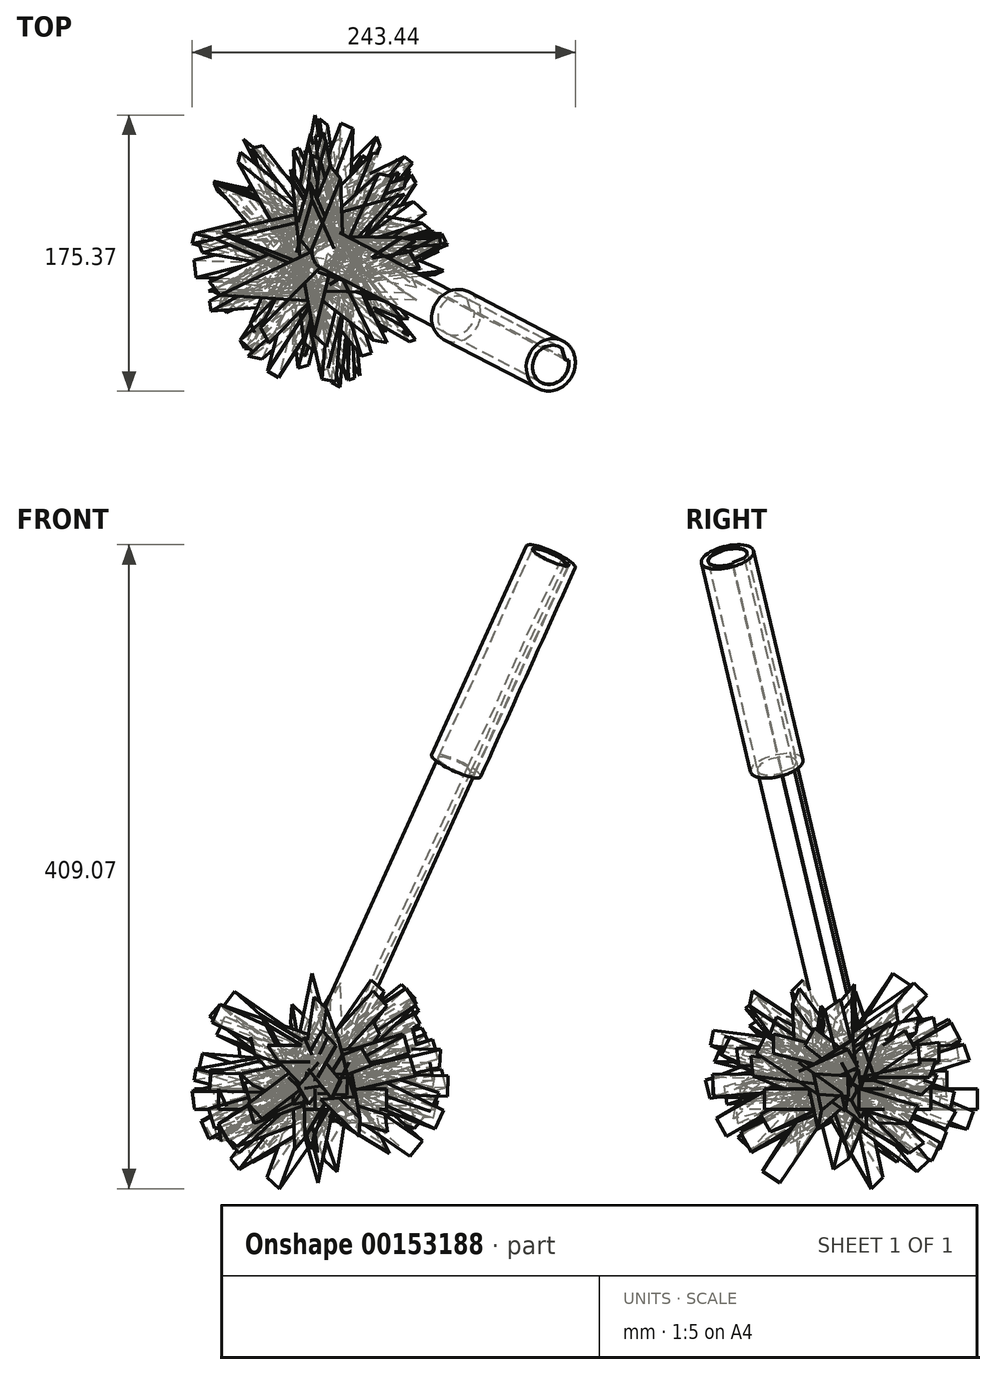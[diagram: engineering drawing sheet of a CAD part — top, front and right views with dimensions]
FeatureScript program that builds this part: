
annotation { "Feature Type Name" : "Feature", "Feature Type Description" : "" }
export const myFeature = defineFeature(function(context is Context, id is Id, definition is map)
    precondition{}
    {
        {
            var Q0;
            Q0=qCreatedBy(makeId("Top.planeOp"),FACE);
            var sketch = newSketch(context, id + "F0", { "sketchPlane" : qUnion([Q0])});
            skCircle(sketch, "E0", {"center": v(0, 0) * mm, "radius": 20.07 * mm});
            skSolve(sketch);
        }
        {
            var Q0;
            Q0=makeQuery(id+"F0.imprint","IMPRINT",FACE,{"disambiguationData":[TD([[makeQuery(id+"F0.imprint","IMPRINT",EDGE,{"derivedFrom":sQuery(id+"F0.wireOp",EDGE,"E0")}),1.0]])]});
            extrude(context, id + "F1", {"entities" : qUnion([Q0]), "depth" : 13.14 * mm});
        }
        {
            var Q0;
            Q0=makeQuery(id+"F1.opExtrude","CAP_FACE",FACE,{"disambiguationData":[OSD([sQuery(id+"F0.wireOp",EDGE,"E0")])],"isStart":false});
            var sketch = newSketch(context, id + "F2", { "sketchPlane" : qUnion([Q0])});
            skLineSegment(sketch, "E1", {"start": v(0, 20.07) * mm, "end": v(0, 75.25) * mm});
            skLineSegment(sketch, "E2", {"start": v(0, 75.25) * mm, "end": v(-12, 16.08) * mm});
            skLineSegment(sketch, "E3", {"start": v(-12, 16.08) * mm, "end": v(12, 16.08) * mm});
            skLineSegment(sketch, "E4", {"start": v(12, 16.08) * mm, "end": v(0, 75.25) * mm});
            skSolve(sketch);
        }
        {
            var Q0;
            {var subQ0=sQuery(id+"F2.wireOp",EDGE,"E1");Q0=makeQuery(id+"F2.imprint","IMPRINT",FACE,{"disambiguationData":[TD([[makeQuery(id+"F2.imprint","IMPRINT",EDGE,{"derivedFrom":subQ0}),1.0]])]});}
            var Q1;
            {var subQ0=sQuery(id+"F2.wireOp",EDGE,"E1");Q1=makeQuery(id+"F2.imprint","IMPRINT",FACE,{"disambiguationData":[TD([[makeQuery(id+"F2.imprint","IMPRINT",EDGE,{"derivedFrom":subQ0}),-1.0]])]});}
            extrude(context, id + "F3", {"entities" : qUnion([Q0, Q1]), "operationType" : NewBodyOperationType.ADD, "oppositeDirection" : true, "depth" : 13.16 * mm});
        }
        {
            var Q0;
            {var subQ0=sQuery(id+"F0.wireOp",EDGE,"E0");Q0=makeQuery(id+"F3.boolean.opBoolean","MERGE",FACE,{"derivedFrom":[makeQuery(id+"F1.opExtrude","CAP_FACE",FACE,{"disambiguationData":[OSD([subQ0])],"isStart":false}),makeQuery(id+"F3.opExtrude","CAP_FACE",FACE,{"disambiguationData":[OSD([subQ0,sQuery(id+"F2.wireOp",EDGE,"E2"),sQuery(id+"F2.wireOp",EDGE,"E4")])],"isStart":true})]});}
            var sketch = newSketch(context, id + "F4", { "sketchPlane" : qUnion([Q0])});
            skLineSegment(sketch, "E5", {"start": v(-12, -16.08) * mm, "end": v(0, -75.25) * mm});
            skLineSegment(sketch, "E6", {"start": v(0, -75.25) * mm, "end": v(12, -16.08) * mm});
            skLineSegment(sketch, "E7", {"start": v(12, -16.08) * mm, "end": v(-12, -16.08) * mm});
            skSolve(sketch);
        }
        {
            var Q0;
            {var subQ0=sQuery(id+"F4.wireOp",EDGE,"E5");Q0=makeQuery(id+"F4.imprint","IMPRINT",FACE,{"disambiguationData":[TD([[makeQuery(id+"F4.imprint","IMPRINT",EDGE,{"derivedFrom":subQ0}),1.0]])]});}
            extrude(context, id + "F5", {"entities" : qUnion([Q0]), "operationType" : NewBodyOperationType.ADD, "oppositeDirection" : true, "depth" : 13.14 * mm});
        }
        {
            var Q0;
            {var subQ0=sQuery(id+"F0.wireOp",EDGE,"E0");Q0=makeQuery(id+"F5.boolean.opBoolean","MERGE",FACE,{"derivedFrom":[makeQuery(id+"F3.boolean.opBoolean","MERGE",FACE,{"derivedFrom":[makeQuery(id+"F1.opExtrude","CAP_FACE",FACE,{"disambiguationData":[OSD([subQ0])],"isStart":false}),makeQuery(id+"F3.opExtrude","CAP_FACE",FACE,{"disambiguationData":[OSD([subQ0,sQuery(id+"F2.wireOp",EDGE,"E2"),sQuery(id+"F2.wireOp",EDGE,"E4")])],"isStart":true})]}),makeQuery(id+"F5.opExtrude","CAP_FACE",FACE,{"disambiguationData":[OSD([subQ0,sQuery(id+"F4.wireOp",EDGE,"E5"),sQuery(id+"F4.wireOp",EDGE,"E6")])],"isStart":true})]});}
            var sketch = newSketch(context, id + "F6", { "sketchPlane" : qUnion([Q0])});
            skLineSegment(sketch, "E8", {"start": v(-12, 16.08) * mm, "end": v(-76.5, 0) * mm});
            skLineSegment(sketch, "E9", {"start": v(-76.5, 0) * mm, "end": v(-12, -16.08) * mm});
            skLineSegment(sketch, "E10", {"start": v(-12, -16.08) * mm, "end": v(-12, 16.08) * mm});
            skSolve(sketch);
        }
        {
            var Q0;
            Q0=makeQuery(id+"F6.imprint","IMPRINT",FACE,{"disambiguationData":[TD([[makeQuery(id+"F6.imprint","IMPRINT",EDGE,{"derivedFrom":sQuery(id+"F6.wireOp",EDGE,"E8")}),1.0]])]});
            extrude(context, id + "F7", {"entities" : qUnion([Q0]), "operationType" : NewBodyOperationType.ADD, "oppositeDirection" : true, "depth" : 13.1 * mm});
        }
        {
            var Q0;
            {var subQ0=sQuery(id+"F0.wireOp",EDGE,"E0");Q0=makeQuery(id+"F7.boolean.opBoolean","MERGE",FACE,{"derivedFrom":[makeQuery(id+"F5.boolean.opBoolean","MERGE",FACE,{"derivedFrom":[makeQuery(id+"F3.boolean.opBoolean","MERGE",FACE,{"derivedFrom":[makeQuery(id+"F1.opExtrude","CAP_FACE",FACE,{"disambiguationData":[OSD([subQ0])],"isStart":false}),makeQuery(id+"F3.opExtrude","CAP_FACE",FACE,{"disambiguationData":[OSD([subQ0,sQuery(id+"F2.wireOp",EDGE,"E2"),sQuery(id+"F2.wireOp",EDGE,"E4")])],"isStart":true})]}),makeQuery(id+"F5.opExtrude","CAP_FACE",FACE,{"disambiguationData":[OSD([subQ0,sQuery(id+"F4.wireOp",EDGE,"E5"),sQuery(id+"F4.wireOp",EDGE,"E6")])],"isStart":true})]}),makeQuery(id+"F7.opExtrude","CAP_FACE",FACE,{"disambiguationData":[OSD([subQ0,sQuery(id+"F6.wireOp",EDGE,"E8"),sQuery(id+"F6.wireOp",EDGE,"E9")])],"isStart":true})]});}
            var sketch = newSketch(context, id + "F8", { "sketchPlane" : qUnion([Q0])});
            skLineSegment(sketch, "E11", {"start": v(12, 16.08) * mm, "end": v(75.98, 0) * mm});
            skLineSegment(sketch, "E12", {"start": v(75.98, 0) * mm, "end": v(12, -16.08) * mm});
            skSolve(sketch);
        }
        {
            var Q0;
            Q0=makeQuery(id+"F8.imprint","IMPRINT",FACE,{"disambiguationData":[TD([[makeQuery(id+"F8.imprint","IMPRINT",EDGE,{"derivedFrom":sQuery(id+"F8.wireOp",EDGE,"E11")}),-1.0]])]});
            extrude(context, id + "F9", {"entities" : qUnion([Q0]), "operationType" : NewBodyOperationType.ADD, "oppositeDirection" : true, "depth" : 13.05 * mm});
        }
        {
            var Q0;
            {var subQ0=sQuery(id+"F0.wireOp",EDGE,"E0");Q0=makeQuery(id+"F9.boolean.opBoolean","MERGE",FACE,{"derivedFrom":[makeQuery(id+"F7.boolean.opBoolean","MERGE",FACE,{"derivedFrom":[makeQuery(id+"F5.boolean.opBoolean","MERGE",FACE,{"derivedFrom":[makeQuery(id+"F3.boolean.opBoolean","MERGE",FACE,{"derivedFrom":[makeQuery(id+"F1.opExtrude","CAP_FACE",FACE,{"disambiguationData":[OSD([subQ0])],"isStart":false}),makeQuery(id+"F3.opExtrude","CAP_FACE",FACE,{"disambiguationData":[OSD([subQ0,sQuery(id+"F2.wireOp",EDGE,"E2"),sQuery(id+"F2.wireOp",EDGE,"E4")])],"isStart":true})]}),makeQuery(id+"F5.opExtrude","CAP_FACE",FACE,{"disambiguationData":[OSD([subQ0,sQuery(id+"F4.wireOp",EDGE,"E5"),sQuery(id+"F4.wireOp",EDGE,"E6")])],"isStart":true})]}),makeQuery(id+"F7.opExtrude","CAP_FACE",FACE,{"disambiguationData":[OSD([subQ0,sQuery(id+"F6.wireOp",EDGE,"E8"),sQuery(id+"F6.wireOp",EDGE,"E9")])],"isStart":true})]}),makeQuery(id+"F9.opExtrude","CAP_FACE",FACE,{"disambiguationData":[OSD([subQ0,sQuery(id+"F8.wireOp",EDGE,"E11"),sQuery(id+"F8.wireOp",EDGE,"E12")])],"isStart":true})]});}
            var sketch = newSketch(context, id + "F10", { "sketchPlane" : qUnion([Q0])});
            skCircle(sketch, "E13", {"center": v(0, 0) * mm, "radius": 20.07 * mm});
            skSolve(sketch);
        }
        {
            var Q0;
            Q0=makeQuery(id+"F1.opExtrude","CAP_FACE",FACE,{"disambiguationData":[OSD([sQuery(id+"F0.wireOp",EDGE,"E0")])],"isStart":true});
            var sketch = newSketch(context, id + "F11", { "sketchPlane" : qUnion([Q0])});
            skCircle(sketch, "E14", {"center": v(0, 0) * mm, "radius": 20.07 * mm});
            skSolve(sketch);
        }
        {
            var Q0;
            Q0=makeQuery(id+"F1.opExtrude","SWEPT_BODY",BODY,{"disambiguationData":[OSD([sQuery(id+"F0.wireOp",EDGE,"E0")])]});
            var Q1;
            Q1=sQuery(id+"F10.wireOp",EDGE,"E13");
            circularPattern(context, id + "F12", {"entities" : qUnion([Q0]), "axis" : qUnion([Q1]), "angle" : 37 * degree, "instanceCount" : 2});
        }
        {
            var Q0;
            Q0=makeQuery(id+"F1.opExtrude","SWEPT_BODY",BODY,{"disambiguationData":[OSD([sQuery(id+"F0.wireOp",EDGE,"E0")])]});
            var Q1;
            Q1=makeQuery(id+"F12.opPattern","COPY",BODY,{"derivedFrom":makeQuery(id+"F1.opExtrude","SWEPT_BODY",BODY,{"disambiguationData":[OSD([sQuery(id+"F0.wireOp",EDGE,"E0")])]}),"instanceName":"1"});
            var Q2;
            Q2=makeQuery(id+"F12.opPattern","COPY",EDGE,{"derivedFrom":makeQuery(id+"F7.opExtrude","CAP_EDGE",EDGE,{"disambiguationData":[OSD([sQuery(id+"F6.wireOp",EDGE,"E8")])],"isStart":true}),"instanceName":"1"});
            circularPattern(context, id + "F13", {"entities" : qUnion([Q0, Q1]), "axis" : qUnion([Q2]), "angle" : 30 * degree, "instanceCount" : 2});
        }
        {
            var Q0;
            Q0=makeQuery(id+"F1.opExtrude","SWEPT_BODY",BODY,{"disambiguationData":[OSD([sQuery(id+"F0.wireOp",EDGE,"E0")])]});
            var Q1;
            Q1=makeQuery(id+"F12.opPattern","COPY",EDGE,{"derivedFrom":makeQuery(id+"F7.opExtrude","CAP_EDGE",EDGE,{"disambiguationData":[OSD([sQuery(id+"F6.wireOp",EDGE,"E9")])],"isStart":false}),"instanceName":"1"});
            circularPattern(context, id + "F14", {"entities" : qUnion([Q0]), "axis" : qUnion([Q1]), "angle" : 30 * degree, "instanceCount" : 2});
        }
        {
            var Q0;
            Q0=makeQuery(id+"F13.opPattern","COPY",BODY,{"derivedFrom":makeQuery(id+"F1.opExtrude","SWEPT_BODY",BODY,{"disambiguationData":[OSD([sQuery(id+"F0.wireOp",EDGE,"E0")])]}),"instanceName":"1"});
            var Q1;
            Q1=sQuery(id+"F11.wireOp",EDGE,"E14");
            circularPattern(context, id + "F15", {"entities" : qUnion([Q0]), "axis" : qUnion([Q1]), "angle" : 30 * degree, "instanceCount" : 2});
        }
        {
            var Q0;
            Q0=makeQuery(id+"F14.opPattern","COPY",BODY,{"derivedFrom":makeQuery(id+"F1.opExtrude","SWEPT_BODY",BODY,{"disambiguationData":[OSD([sQuery(id+"F0.wireOp",EDGE,"E0")])]}),"instanceName":"1"});
            var Q1;
            Q1=makeQuery(id+"F12.opPattern","COPY",EDGE,{"derivedFrom":makeQuery(id+"F5.opExtrude","CAP_EDGE",EDGE,{"disambiguationData":[OSD([sQuery(id+"F4.wireOp",EDGE,"E6")])],"isStart":true}),"instanceName":"1"});
            circularPattern(context, id + "F16", {"entities" : qUnion([Q0]), "axis" : qUnion([Q1]), "angle" : 30 * degree, "instanceCount" : 2});
        }
        {
            var Q0;
            Q0=makeQuery(id+"F16.opPattern","COPY",BODY,{"derivedFrom":makeQuery(id+"F14.opPattern","COPY",BODY,{"derivedFrom":makeQuery(id+"F1.opExtrude","SWEPT_BODY",BODY,{"disambiguationData":[OSD([sQuery(id+"F0.wireOp",EDGE,"E0")])]}),"instanceName":"1"}),"instanceName":"1"});
            var Q1;
            Q1=makeQuery(id+"F13.opPattern","COPY",BODY,{"derivedFrom":makeQuery(id+"F12.opPattern","COPY",BODY,{"derivedFrom":makeQuery(id+"F1.opExtrude","SWEPT_BODY",BODY,{"disambiguationData":[OSD([sQuery(id+"F0.wireOp",EDGE,"E0")])]}),"instanceName":"1"}),"instanceName":"1"});
            var Q2;
            Q2=makeQuery(id+"F13.opPattern","COPY",BODY,{"derivedFrom":makeQuery(id+"F1.opExtrude","SWEPT_BODY",BODY,{"disambiguationData":[OSD([sQuery(id+"F0.wireOp",EDGE,"E0")])]}),"instanceName":"1"});
            var Q3;
            Q3=makeQuery(id+"F14.opPattern","COPY",BODY,{"derivedFrom":makeQuery(id+"F1.opExtrude","SWEPT_BODY",BODY,{"disambiguationData":[OSD([sQuery(id+"F0.wireOp",EDGE,"E0")])]}),"instanceName":"1"});
            var Q4;
            Q4=makeQuery(id+"F12.opPattern","COPY",BODY,{"derivedFrom":makeQuery(id+"F1.opExtrude","SWEPT_BODY",BODY,{"disambiguationData":[OSD([sQuery(id+"F0.wireOp",EDGE,"E0")])]}),"instanceName":"1"});
            var Q5;
            Q5=makeQuery(id+"F1.opExtrude","SWEPT_BODY",BODY,{"disambiguationData":[OSD([sQuery(id+"F0.wireOp",EDGE,"E0")])]});
            var Q6;
            Q6=makeQuery(id+"F15.opPattern","COPY",BODY,{"derivedFrom":makeQuery(id+"F13.opPattern","COPY",BODY,{"derivedFrom":makeQuery(id+"F1.opExtrude","SWEPT_BODY",BODY,{"disambiguationData":[OSD([sQuery(id+"F0.wireOp",EDGE,"E0")])]}),"instanceName":"1"}),"instanceName":"1"});
            var Q7;
            Q7=makeQuery(id+"F7.opExtrude","CAP_EDGE",EDGE,{"disambiguationData":[OSD([sQuery(id+"F6.wireOp",EDGE,"E9")])],"isStart":false});
            circularPattern(context, id + "F17", {"entities" : qUnion([Q0, Q1, Q2, Q3, Q4, Q5, Q6]), "axis" : qUnion([Q7]), "angle" : 30 * degree, "instanceCount" : 2});
        }
        {
            var Q0;
            Q0=makeQuery(id+"F13.opPattern","COPY",BODY,{"derivedFrom":makeQuery(id+"F12.opPattern","COPY",BODY,{"derivedFrom":makeQuery(id+"F1.opExtrude","SWEPT_BODY",BODY,{"disambiguationData":[OSD([sQuery(id+"F0.wireOp",EDGE,"E0")])]}),"instanceName":"1"}),"instanceName":"1"});
            var Q1;
            Q1=makeQuery(id+"F12.opPattern","COPY",BODY,{"derivedFrom":makeQuery(id+"F1.opExtrude","SWEPT_BODY",BODY,{"disambiguationData":[OSD([sQuery(id+"F0.wireOp",EDGE,"E0")])]}),"instanceName":"1"});
            var Q2;
            Q2=makeQuery(id+"F17.opPattern","COPY",BODY,{"derivedFrom":makeQuery(id+"F12.opPattern","COPY",BODY,{"derivedFrom":makeQuery(id+"F1.opExtrude","SWEPT_BODY",BODY,{"disambiguationData":[OSD([sQuery(id+"F0.wireOp",EDGE,"E0")])]}),"instanceName":"1"}),"instanceName":"1"});
            var Q3;
            Q3=makeQuery(id+"F16.opPattern","COPY",BODY,{"derivedFrom":makeQuery(id+"F14.opPattern","COPY",BODY,{"derivedFrom":makeQuery(id+"F1.opExtrude","SWEPT_BODY",BODY,{"disambiguationData":[OSD([sQuery(id+"F0.wireOp",EDGE,"E0")])]}),"instanceName":"1"}),"instanceName":"1"});
            var Q4;
            Q4=makeQuery(id+"F17.opPattern","COPY",BODY,{"derivedFrom":makeQuery(id+"F13.opPattern","COPY",BODY,{"derivedFrom":makeQuery(id+"F1.opExtrude","SWEPT_BODY",BODY,{"disambiguationData":[OSD([sQuery(id+"F0.wireOp",EDGE,"E0")])]}),"instanceName":"1"}),"instanceName":"1"});
            var Q5;
            Q5=makeQuery(id+"F14.opPattern","COPY",BODY,{"derivedFrom":makeQuery(id+"F1.opExtrude","SWEPT_BODY",BODY,{"disambiguationData":[OSD([sQuery(id+"F0.wireOp",EDGE,"E0")])]}),"instanceName":"1"});
            var Q6;
            Q6=makeQuery(id+"F17.opPattern","COPY",BODY,{"derivedFrom":makeQuery(id+"F16.opPattern","COPY",BODY,{"derivedFrom":makeQuery(id+"F14.opPattern","COPY",BODY,{"derivedFrom":makeQuery(id+"F1.opExtrude","SWEPT_BODY",BODY,{"disambiguationData":[OSD([sQuery(id+"F0.wireOp",EDGE,"E0")])]}),"instanceName":"1"}),"instanceName":"1"}),"instanceName":"1"});
            var Q7;
            Q7=makeQuery(id+"F17.opPattern","COPY",BODY,{"derivedFrom":makeQuery(id+"F14.opPattern","COPY",BODY,{"derivedFrom":makeQuery(id+"F1.opExtrude","SWEPT_BODY",BODY,{"disambiguationData":[OSD([sQuery(id+"F0.wireOp",EDGE,"E0")])]}),"instanceName":"1"}),"instanceName":"1"});
            var Q8;
            Q8=makeQuery(id+"F17.opPattern","COPY",BODY,{"derivedFrom":makeQuery(id+"F1.opExtrude","SWEPT_BODY",BODY,{"disambiguationData":[OSD([sQuery(id+"F0.wireOp",EDGE,"E0")])]}),"instanceName":"1"});
            var Q9;
            Q9=makeQuery(id+"F17.opPattern","COPY",BODY,{"derivedFrom":makeQuery(id+"F13.opPattern","COPY",BODY,{"derivedFrom":makeQuery(id+"F12.opPattern","COPY",BODY,{"derivedFrom":makeQuery(id+"F1.opExtrude","SWEPT_BODY",BODY,{"disambiguationData":[OSD([sQuery(id+"F0.wireOp",EDGE,"E0")])]}),"instanceName":"1"}),"instanceName":"1"}),"instanceName":"1"});
            var Q10;
            Q10=makeQuery(id+"F17.opPattern","COPY",BODY,{"derivedFrom":makeQuery(id+"F15.opPattern","COPY",BODY,{"derivedFrom":makeQuery(id+"F13.opPattern","COPY",BODY,{"derivedFrom":makeQuery(id+"F1.opExtrude","SWEPT_BODY",BODY,{"disambiguationData":[OSD([sQuery(id+"F0.wireOp",EDGE,"E0")])]}),"instanceName":"1"}),"instanceName":"1"}),"instanceName":"1"});
            var Q11;
            Q11=makeQuery(id+"F15.opPattern","COPY",BODY,{"derivedFrom":makeQuery(id+"F13.opPattern","COPY",BODY,{"derivedFrom":makeQuery(id+"F1.opExtrude","SWEPT_BODY",BODY,{"disambiguationData":[OSD([sQuery(id+"F0.wireOp",EDGE,"E0")])]}),"instanceName":"1"}),"instanceName":"1"});
            var Q12;
            Q12=makeQuery(id+"F13.opPattern","COPY",BODY,{"derivedFrom":makeQuery(id+"F1.opExtrude","SWEPT_BODY",BODY,{"disambiguationData":[OSD([sQuery(id+"F0.wireOp",EDGE,"E0")])]}),"instanceName":"1"});
            var Q13;
            Q13=makeQuery(id+"F1.opExtrude","SWEPT_BODY",BODY,{"disambiguationData":[OSD([sQuery(id+"F0.wireOp",EDGE,"E0")])]});
            var Q14;
            Q14=makeQuery(id+"F17.opPattern","COPY",EDGE,{"derivedFrom":makeQuery(id+"F16.opPattern","COPY",EDGE,{"derivedFrom":makeQuery(id+"F14.opPattern","COPY",EDGE,{"derivedFrom":makeQuery(id+"F7.opExtrude","CAP_EDGE",EDGE,{"disambiguationData":[OSD([sQuery(id+"F6.wireOp",EDGE,"E8")])],"isStart":true}),"instanceName":"1"}),"instanceName":"1"}),"instanceName":"1"});
            circularPattern(context, id + "F18", {"entities" : qUnion([Q0, Q1, Q2, Q3, Q4, Q5, Q6, Q7, Q8, Q9, Q10, Q11, Q12, Q13]), "axis" : qUnion([Q14]), "angle" : 30 * degree, "instanceCount" : 2});
        }
        {
            var Q0;
            {var subQ0=sQuery(id+"F0.wireOp",EDGE,"E0");Q0=makeQuery(id+"F18.opPattern","COPY",FACE,{"derivedFrom":makeQuery(id+"F17.opPattern","COPY",FACE,{"derivedFrom":makeQuery(id+"F16.opPattern","COPY",FACE,{"derivedFrom":makeQuery(id+"F14.opPattern","COPY",FACE,{"derivedFrom":makeQuery(id+"F9.boolean.opBoolean","MERGE",FACE,{"derivedFrom":[makeQuery(id+"F7.boolean.opBoolean","MERGE",FACE,{"derivedFrom":[makeQuery(id+"F5.boolean.opBoolean","MERGE",FACE,{"derivedFrom":[makeQuery(id+"F3.boolean.opBoolean","MERGE",FACE,{"derivedFrom":[makeQuery(id+"F1.opExtrude","CAP_FACE",FACE,{"disambiguationData":[OSD([subQ0])],"isStart":false}),makeQuery(id+"F3.opExtrude","CAP_FACE",FACE,{"disambiguationData":[OSD([subQ0,sQuery(id+"F2.wireOp",EDGE,"E2"),sQuery(id+"F2.wireOp",EDGE,"E4")])],"isStart":true})]}),makeQuery(id+"F5.opExtrude","CAP_FACE",FACE,{"disambiguationData":[OSD([subQ0,sQuery(id+"F4.wireOp",EDGE,"E5"),sQuery(id+"F4.wireOp",EDGE,"E6")])],"isStart":true})]}),makeQuery(id+"F7.opExtrude","CAP_FACE",FACE,{"disambiguationData":[OSD([subQ0,sQuery(id+"F6.wireOp",EDGE,"E8"),sQuery(id+"F6.wireOp",EDGE,"E9")])],"isStart":true})]}),makeQuery(id+"F9.opExtrude","CAP_FACE",FACE,{"disambiguationData":[OSD([subQ0,sQuery(id+"F8.wireOp",EDGE,"E11"),sQuery(id+"F8.wireOp",EDGE,"E12")])],"isStart":true})]}),"instanceName":"1"}),"instanceName":"1"}),"instanceName":"1"}),"instanceName":"1"});}
            var sketch = newSketch(context, id + "F19", { "sketchPlane" : qUnion([Q0])});
            skCircle(sketch, "E15", {"center": v(-8.46, -0.72) * mm, "radius": 12.71 * mm});
            skSolve(sketch);
        }
        {
            var Q0;
            {var subQ0=sQuery(id+"F19.wireOp",EDGE,"E15");var subQ1=makeQuery(id+"F18.opPattern","COPY",EDGE,{"derivedFrom":makeQuery(id+"F17.opPattern","COPY",EDGE,{"derivedFrom":makeQuery(id+"F16.opPattern","COPY",EDGE,{"derivedFrom":makeQuery(id+"F14.opPattern","COPY",EDGE,{"derivedFrom":makeQuery(id+"F3.opExtrude","CAP_EDGE",EDGE,{"disambiguationData":[OSD([sQuery(id+"F2.wireOp",EDGE,"E4")])],"isStart":true}),"instanceName":"1"}),"instanceName":"1"}),"instanceName":"1"}),"instanceName":"1"});var subQ2=makeQuery(id+"F19.imprint","INTERSECT",VERTEX,{"derivedFrom":[subQ1,subQ0]});Q0=makeQuery(id+"F19.imprint","IMPRINT",FACE,{"disambiguationData":[TD([[makeQuery(id+"F19.imprint","IMPRINT",EDGE,{"disambiguationData":[TD([[subQ2,-1.0]])],"derivedFrom":subQ0}),1.0]])]});}
            extrude(context, id + "F20", {"entities" : qUnion([Q0]), "depth" : 198.02 * mm});
        }
        {
            var Q0;
            Q0=makeQuery(id+"F20.opExtrude","CAP_FACE",FACE,{"disambiguationData":[OSD([sQuery(id+"F2.wireOp",EDGE,"E4"),sQuery(id+"F8.wireOp",EDGE,"E11"),sQuery(id+"F19.wireOp",EDGE,"E15")])],"isStart":false});
            var sketch = newSketch(context, id + "F21", { "sketchPlane" : qUnion([Q0])});
            skCircle(sketch, "E16", {"center": v(-8.46, -0.72) * mm, "radius": 17.05 * mm});
            skSolve(sketch);
        }
        {
            var Q0;
            Q0=makeQuery(id+"F21.imprint","IMPRINT",FACE,{"disambiguationData":[TD([[makeQuery(id+"F21.imprint","IMPRINT",EDGE,{"derivedFrom":sQuery(id+"F21.wireOp",EDGE,"E16")}),1.0]])]});
            extrude(context, id + "F22", {"entities" : qUnion([Q0]), "depth" : 149.08 * mm});
        }
        {
            var Q0;
            Q0=makeQuery(id+"F20.opExtrude","CAP_FACE",FACE,{"disambiguationData":[OSD([sQuery(id+"F2.wireOp",EDGE,"E4"),sQuery(id+"F8.wireOp",EDGE,"E11"),sQuery(id+"F19.wireOp",EDGE,"E15")])],"isStart":false});
            extrude(context, id + "F23", {"entities" : qUnion([Q0]), "depth" : 148.4 * mm});
        }
    });
